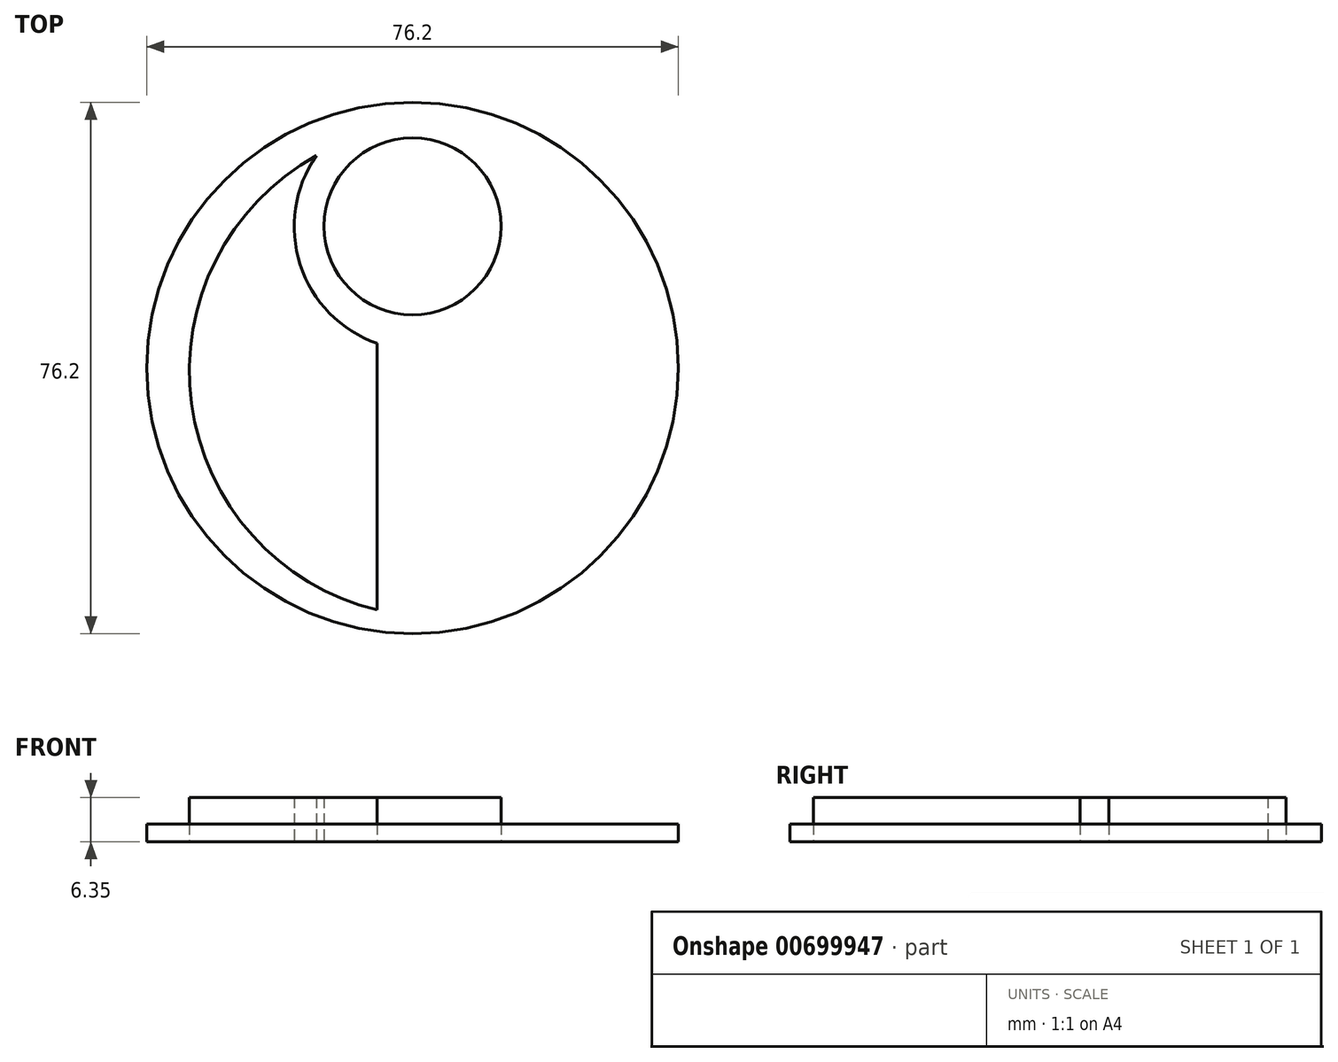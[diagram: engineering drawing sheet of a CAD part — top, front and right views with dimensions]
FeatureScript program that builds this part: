
annotation { "Feature Type Name" : "Feature", "Feature Type Description" : "" }
export const myFeature = defineFeature(function(context is Context, id is Id, definition is map)
    precondition{}
    {
        {
            var Q0;
            Q0=qCreatedBy(makeId("Top.planeOp"),FACE);
            var sketch = newSketch(context, id + "F0", { "sketchPlane" : qUnion([Q0])});
            skCircle(sketch, "E0", {"center": v(0, 25.4) * mm, "radius": 12.7 * mm});
            skArc(sketch, "E1", {"start": v(-13.77, 35.52) * mm, "mid": v(-15.13, 17.5) * mm, "end": v(0, 7.62) * mm});
            skArc(sketch, "E2.MirrorCS", {"start": v(13.77, 35.52) * mm, "mid": v(15.13, 17.5) * mm, "end": v(0, 7.62) * mm});
            skArc(sketch, "E3", {"start": v(0, -30.48) * mm, "mid": v(31.25, -2.56) * mm, "end": v(13.77, 35.52) * mm});
            skArc(sketch, "E4.MirrorCS", {"start": v(0, -30.48) * mm, "mid": v(-31.25, -2.56) * mm, "end": v(-13.77, 35.52) * mm});
            skLineSegment(sketch, "E5", {"start": v(0, -48.37) * mm, "end": v(5.08, -48.37) * mm});
            skLineSegment(sketch, "E6.MirrorCS", {"start": v(0, -48.37) * mm, "end": v(-5.08, -48.37) * mm});
            skLineSegment(sketch, "E7", {"start": v(5.08, -48.37) * mm, "end": v(5.08, 10.05) * mm});
            skLineSegment(sketch, "E8.MirrorCS", {"start": v(-5.08, -48.37) * mm, "end": v(-5.08, 10.05) * mm});
            skLineSegment(sketch, "E9", {"start": v(-5.08, 10.05) * mm, "end": v(5.08, 10.05) * mm});
            skSolve(sketch);
        }
        {
            var Q0;
            {var subQ0=sQuery(id+"F0.wireOp",EDGE,"E3");var subQ1=sQuery(id+"F0.wireOp",EDGE,"E2.MirrorCS");var subQ2=makeQuery(id+"F0.imprint","INTERSECT",VERTEX,{"derivedFrom":[subQ1,subQ0]});Q0=makeQuery(id+"F0.imprint","IMPRINT",FACE,{"disambiguationData":[TD([[makeQuery(id+"F0.imprint","IMPRINT",EDGE,{"disambiguationData":[TD([[subQ2,-1.0]])],"derivedFrom":subQ1}),1.0]])]});}
            var Q1;
            {var subQ0=sQuery(id+"F0.wireOp",EDGE,"E4.MirrorCS");var subQ1=sQuery(id+"F0.wireOp",EDGE,"E1");var subQ2=makeQuery(id+"F0.imprint","INTERSECT",VERTEX,{"derivedFrom":[subQ1,subQ0]});Q1=makeQuery(id+"F0.imprint","IMPRINT",FACE,{"disambiguationData":[TD([[makeQuery(id+"F0.imprint","IMPRINT",EDGE,{"disambiguationData":[TD([[subQ2,-1.0]])],"derivedFrom":subQ1}),-1.0]])]});}
            var Q2;
            Q2=makeQuery(id+"F0.imprint","IMPRINT",FACE,{"disambiguationData":[TD([[makeQuery(id+"F0.imprint","IMPRINT",EDGE,{"derivedFrom":sQuery(id+"F0.wireOp",EDGE,"E0")}),1.0]])]});
            extrude(context, id + "F1", {"entities" : qUnion([Q0, Q1, Q2]), "depth" : 6.35 * mm, "offsetDistance" : 25.4 * mm});
        }
        {
            var Q0;
            Q0=qCreatedBy(makeId("Top.planeOp"),FACE);
            var sketch = newSketch(context, id + "F2", { "sketchPlane" : qUnion([Q0])});
            skCircle(sketch, "E10", {"center": v(0, 5.08) * mm, "radius": 38.1 * mm});
            skSolve(sketch);
        }
        {
            var Q0;
            Q0=makeQuery(id+"F2.imprint","IMPRINT",FACE,{"disambiguationData":[TD([[makeQuery(id+"F2.imprint","IMPRINT",EDGE,{"derivedFrom":sQuery(id+"F2.wireOp",EDGE,"E10")}),1.0]])]});
            extrude(context, id + "F3", {"entities" : qUnion([Q0]), "depth" : 2.54 * mm, "offsetDistance" : 25.4 * mm});
        }
    });
